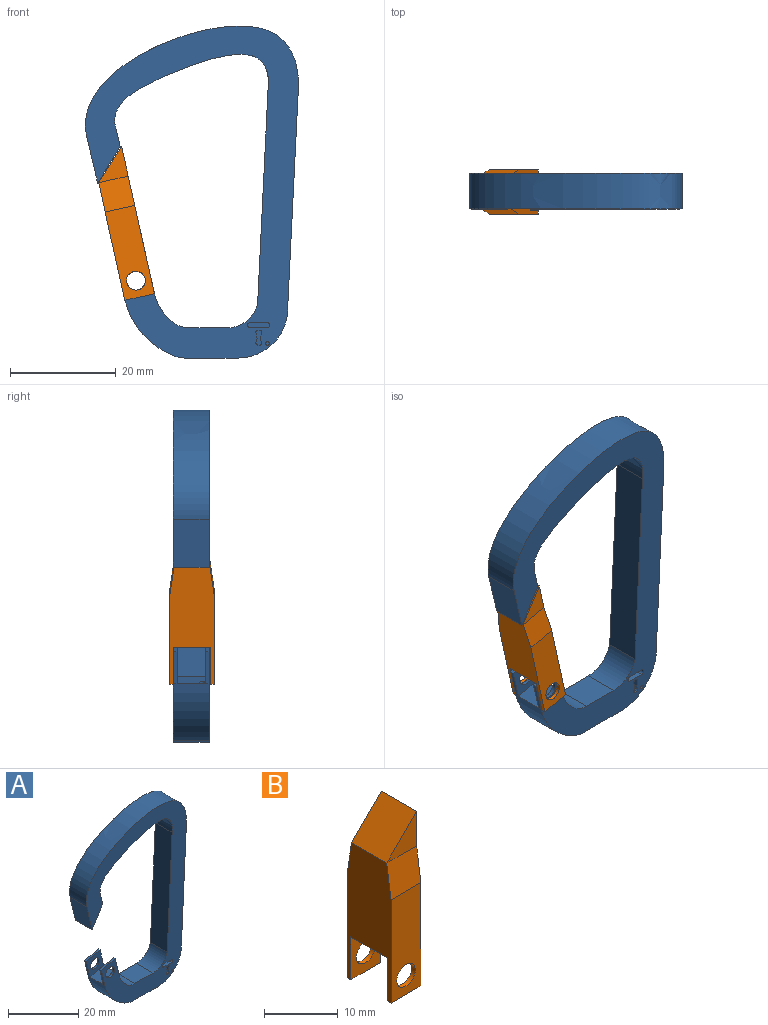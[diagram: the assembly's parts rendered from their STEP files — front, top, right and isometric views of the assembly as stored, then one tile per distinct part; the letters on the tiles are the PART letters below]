
ASSEMBLY  parts=2 mates=2
PART A: 48 faces, bbox 41.2x6.8x63.5 mm
  f0: plane 63.54x41.25mm, normal (0,-1,0), area 755.4mm2, adj f1,f2,f3,f5,f6,f7,f8,f9
  f1: plane 6.06x1.42mm, normal (0.97,0,0.23), area 4.3mm2, adj f0,f2,f13,f24
  f2: plane 5.57x1.3mm, normal (-0.23,0,0.97), area 4mm2, adj f0,f1,f3,f24
  f3: plane 6.06x1.42mm, normal (-0.97,0,-0.23), area 4.3mm2, adj f0,f2,f14,f24
  f4: cylinder r=1.78mm len=3.56mm, axis (0,-1,0), area 7.8mm2, adj f15,f23
  f5: plane 10.13x6.76mm, normal (0,0,-1), area 68.4mm2, adj f0,f6,f15,f47
  f6: cylinder r=9.39mm len=9.86mm, axis (0,-1,0), area 102.8mm2, adj f0,f5,f7,f15
  f7: plane 40.72x6.76mm, normal (1,0,-0.05), area 275.5mm2, adj f0,f6,f8,f15
  f8: extruded ~40.28x20.65mm, area 394.7mm2, adj f0,f7,f15,f19
  f9: extruded ~29.04x13.98mm, area 267.8mm2, adj f0,f10,f15,f21
  f10: plane 40.72x6.76mm, normal (-1,0,0.05), area 275.5mm2, adj f0,f9,f11,f15
  f11: cylinder r=5.88mm len=6.76mm, axis (0,-1,0), area 52.4mm2, adj f0,f10,f12,f15
  f12: plane 7.3x6.76mm, normal (0,0,1), area 49.3mm2, adj f0,f11,f15,f46
  f13: cylinder r=10.26mm len=6.76mm, axis (0,-1,0), area 42mm2, adj f0,f1,f15,f16,f25,f46
  f14: cylinder r=14.98mm len=10.71mm, axis (0,-1,0), area 101.2mm2, adj f0,f3,f15,f18,f25,f47
  f15: plane 63.54x41.25mm, normal (0,1,0), area 762.3mm2, adj f4,f5,f6,f7,f8,f9,f10,f11
  f16: plane 6.06x1.42mm, normal (0.97,0,0.23), area 4.3mm2, adj f13,f15,f17,f23
  f17: plane 5.57x1.3mm, normal (-0.23,0,0.97), area 4mm2, adj f15,f16,f18,f23
  f18: plane 6.06x1.42mm, normal (-0.97,0,-0.23), area 4.3mm2, adj f14,f15,f17,f23
  f19: plane 9.03x6.76mm, normal (-0.97,0,-0.23), area 62.6mm2, adj f0,f8,f15,f20
  f20: plane 6.87x6.76mm, normal (0.85,0,-0.53), area 54.6mm2, adj f0,f15,f19,f21
  f21: plane 6.76x3.46mm, normal (0.97,0,0.23), area 24mm2, adj f0,f9,f15,f20
  f22: cylinder r=1.78mm len=3.56mm, axis (0,-1,0), area 7.8mm2, adj f0,f24
  f23: plane 7.36x6.98mm, normal (0,-1,0), area 25.6mm2, adj f4,f16,f17,f18,f25
  f24: plane 7.36x6.98mm, normal (0,1,0), area 25.6mm2, adj f1,f2,f3,f22,f25
  f25: plane 5.57x5.36mm, normal (-0.23,0,0.97), area 29.5mm2, adj f13,f14,f23,f24,f44
  f26: plane 3.05x1.11mm, normal (0.97,0,0.24), area 3.5mm2, adj f0,f27,f35,f36
  f27: plane 3.05x0.81mm, normal (0.96,0,-0.29), area 2.6mm2, adj f0,f26,f28,f36
  f28: extruded ~3.05x0.48mm, area 2mm2, adj f0,f27,f29,f36
  f29: plane 3.05x0.36mm, normal (0,0,1), area 1.1mm2, adj f0,f28,f30,f36
  f30: extruded ~3.05x0.48mm, area 2mm2, adj f0,f29,f31,f36
  f31: plane 3.05x0.81mm, normal (-0.96,0,-0.29), area 2.6mm2, adj f0,f30,f32,f36
  f32: plane 3.05x1.11mm, normal (-0.97,0,0.24), area 3.5mm2, adj f0,f31,f33,f36
  f33: extruded ~3.05x0.46mm, area 2mm2, adj f0,f32,f34,f36
  f34: plane 3.05x0.36mm, normal (0,0,-1), area 1.1mm2, adj f0,f33,f35,f36
  f35: extruded ~3.05x0.46mm, area 2mm2, adj f0,f26,f34,f36
  f36: plane 2.86x1.14mm, normal (0,-1,0), area 2.4mm2, adj f26,f27,f28,f29,f30,f31,f32,f33
  f37: cylinder r=0.35mm len=3.05mm, axis (0,-1,0), area 6.7mm2, adj f0,f38
  f38: plane 0.7x0.7mm, normal (0,-1,0), area 0.4mm2, adj f37
  f39: plane 3.21x3.05mm, normal (0,0,-1), area 9.8mm2, adj f0,f40,f42,f43
  f40: cylinder r=0.52mm len=3.05mm, axis (0,-1,0), area 4.6mm2, adj f0,f39,f41,f43
  f41: plane 3.21x3.05mm, normal (0,0,1), area 9.8mm2, adj f0,f40,f42,f43
  f42: cylinder r=0.51mm len=3.05mm, axis (0,-1,0), area 4.7mm2, adj f0,f39,f41,f43
  f43: plane 4.15x1.03mm, normal (0,-1,0), area 4mm2, adj f39,f40,f41,f42
  f44: cylinder r=0.6mm len=2.74mm, axis (-0.23,0,0.97), area 9.5mm2, adj f25,f45
  f45: plane 1.19x1.16mm, normal (-0.23,0,0.97), area 1.1mm2, adj f44
  f46: cylinder r=5.08mm len=6.76mm, axis (0,-1,0), area 25.2mm2, adj f0,f12,f13,f15
  f47: cylinder r=5.08mm len=6.76mm, axis (0,-1,0), area 11.7mm2, adj f0,f5,f14,f15
PART B: 18 faces, bbox 5.7x8.4x28.5 mm
  f0: plane 6.76x5.72mm, normal (-0.71,0,0.71), area 54.6mm2, adj f1,f3,f12,f14
  f1: plane 22.78x8.41mm, normal (-1,0,0), area 137mm2, adj f0,f2,f5,f6,f7,f9,f10,f11
  f2: plane 5.72x0.7mm, normal (0,0,-1), area 4mm2, adj f1,f3,f6,f10
  f3: plane 28.5x8.41mm, normal (1,0,0), area 175.6mm2, adj f0,f2,f5,f6,f7,f9,f10,f11
  f4: cylinder r=1.78mm len=3.56mm, axis (0,-1,0), area 7.8mm2, adj f6,f10
  f5: plane 5.72x0.7mm, normal (0,0,-1), area 4mm2, adj f1,f3,f7,f11
  f6: plane 17.11x5.72mm, normal (0,1,0), area 87.8mm2, adj f1,f2,f3,f4,f13
  f7: plane 17.11x5.72mm, normal (0,-1,0), area 87.8mm2, adj f1,f3,f5,f8,f15
  f8: cylinder r=1.78mm len=3.56mm, axis (0,-1,0), area 7.8mm2, adj f7,f11
  f9: plane 7.01x5.72mm, normal (0,0,-1), area 38.9mm2, adj f1,f3,f10,f11,f16
  f10: plane 7.11x5.72mm, normal (0,-1,0), area 30.7mm2, adj f1,f2,f3,f4,f9
  f11: plane 7.11x5.72mm, normal (0,1,0), area 30.7mm2, adj f1,f3,f5,f8,f9
  f12: plane 5.72x5.72mm, normal (0,1,0), area 16.3mm2, adj f0,f3,f13
  f13: plane 5.72x5.68mm, normal (0,0.99,0.14), area 32.8mm2, adj f1,f3,f6,f12
  f14: plane 5.72x5.72mm, normal (0,-1,0), area 16.3mm2, adj f0,f3,f15
  f15: plane 5.72x5.68mm, normal (0,-0.99,0.14), area 32.8mm2, adj f1,f3,f7,f14
  f16: cylinder r=0.6mm len=12.7mm, axis (0,0,-1), area 47.5mm2, adj f9,f17
  f17: plane 1.19x1.19mm, normal (0,0,-1), area 1.1mm2, adj f16
PLACE A t=(36.72,1.97,7.67)mm
PLACE B rot(axis=(0,-1,0),12.6deg) t=(16.25,1.02,-2.38)mm
MATE cylindrical B.f4 <-> A.f4  axis (0,-1,0) through (19.43,9.08,-3.54)mm
MATE planar B.f10 <-> A.f15  axis (0,-1,0) through (19.32,8.73,-3.05)mm
